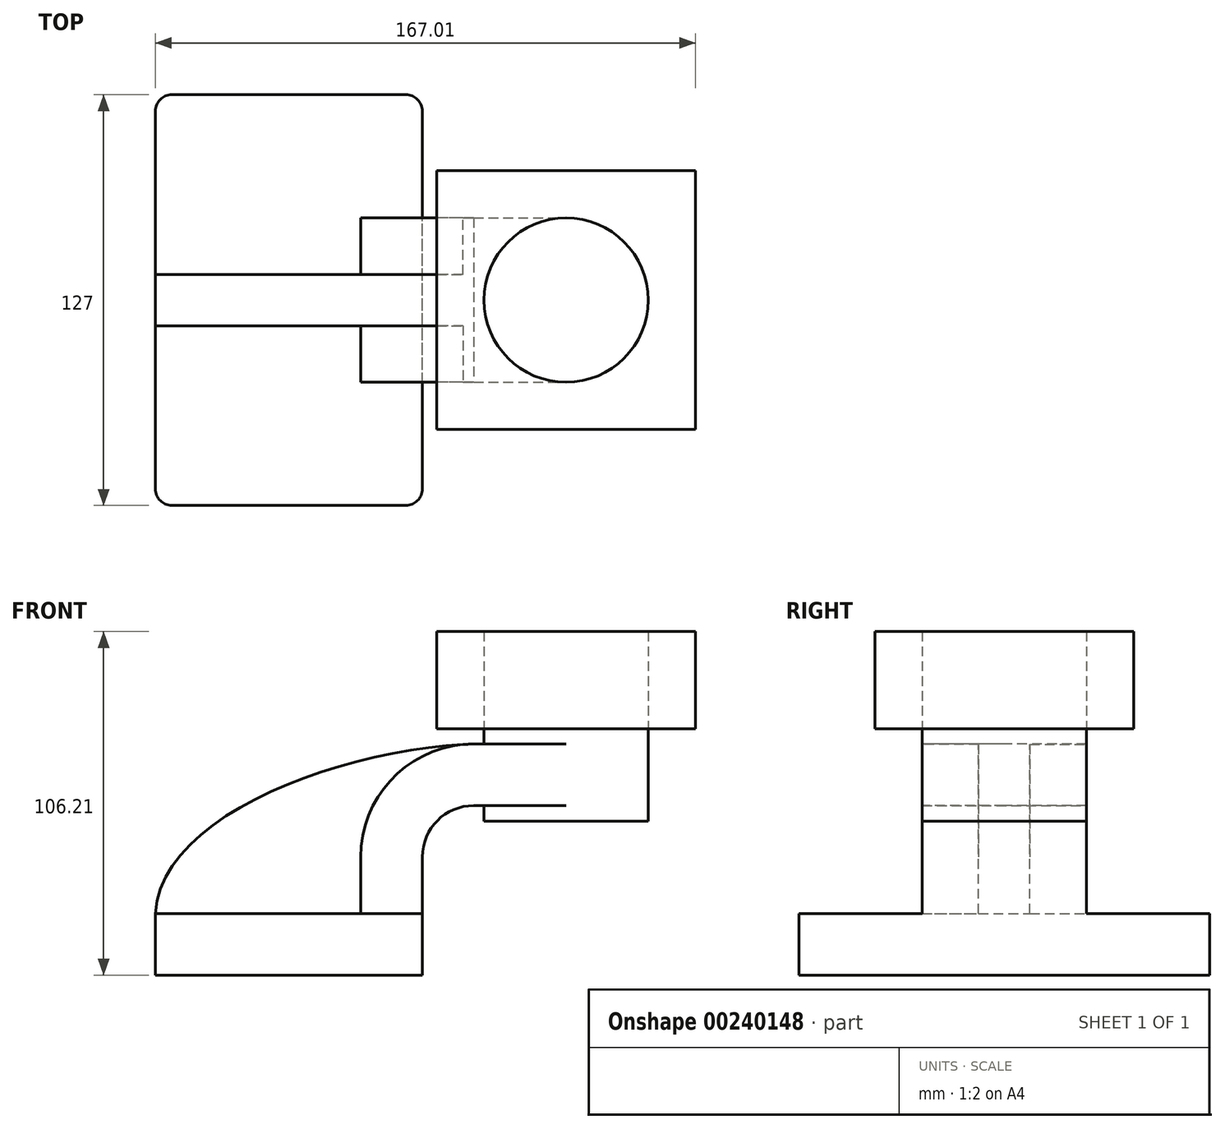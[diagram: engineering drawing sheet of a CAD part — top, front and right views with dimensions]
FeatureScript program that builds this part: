
annotation { "Feature Type Name" : "Feature", "Feature Type Description" : "" }
export const myFeature = defineFeature(function(context is Context, id is Id, definition is map)
    precondition{}
    {
        {
            var Q0;
            Q0=qCreatedBy(makeId("Front.planeOp"),FACE);
            var sketch = newSketch(context, id + "F0", { "sketchPlane" : qUnion([Q0])});
            skLineSegment(sketch, "E0.rect.bottom", {"start": v(-41.28, 9.52) * mm, "end": v(41.28, 9.52) * mm});
            skLineSegment(sketch, "E0.rect.top", {"start": v(-41.28, -9.52) * mm, "end": v(41.28, -9.52) * mm});
            skLineSegment(sketch, "E0.rect.left", {"start": v(-41.28, 9.52) * mm, "end": v(-41.28, -9.52) * mm});
            skLineSegment(sketch, "E0.rect.right", {"start": v(41.28, 9.52) * mm, "end": v(41.28, -9.52) * mm});
            skPoint(sketch, "E0.rect.middle", {"position": v(0, 0) * mm});
            skLineSegment(sketch, "E1", {"start": v(41.28, 9.52) * mm, "end": v(41.28, 27) * mm});
            skArc(sketch, "E2", {"start": v(41.28, 27) * mm, "mid": v(45.92, 38.23) * mm, "end": v(57.15, 42.88) * mm});
            skLineSegment(sketch, "E3", {"start": v(57.15, 42.88) * mm, "end": v(85.72, 42.88) * mm});
            skLineSegment(sketch, "E4.rect.bottom", {"start": v(60.32, 38.1) * mm, "end": v(111.12, 38.1) * mm});
            skLineSegment(sketch, "E4.rect.top", {"start": v(60.32, 66.68) * mm, "end": v(111.12, 66.68) * mm});
            skLineSegment(sketch, "E4.rect.left", {"start": v(60.32, 38.1) * mm, "end": v(60.32, 66.68) * mm});
            skLineSegment(sketch, "E4.rect.right", {"start": v(111.13, 38.1) * mm, "end": v(111.12, 66.68) * mm});
            skPoint(sketch, "E4.rect.middle", {"position": v(85.72, 52.39) * mm});
            skLineSegment(sketch, "E5.0", {"start": v(57.15, 61.93) * mm, "end": v(85.72, 61.93) * mm});
            skArc(sketch, "E5.1", {"start": v(22.23, 27) * mm, "mid": v(32.45, 51.7) * mm, "end": v(57.15, 61.93) * mm});
            skLineSegment(sketch, "E5.2", {"start": v(22.23, 9.52) * mm, "end": v(22.23, 27) * mm});
            skLineSegment(sketch, "E6", {"start": v(85.72, 38.1) * mm, "end": v(85.72, 66.68) * mm});
            skFitSpline(sketch, "E7", {"points": [v(-41.28, 9.53) * mm, v(57.15, 61.93) * mm], "startDerivative": vector(5.2, 92.34) * mm, "endDerivative": vector(120.92, 4.22) * mm});
            skSolve(sketch);
        }
        {
            var Q0;
            Q0=makeQuery(id+"F0.imprint","IMPRINT",FACE,{"disambiguationData":[TD([[makeQuery(id+"F0.imprint","IMPRINT",EDGE,{"derivedFrom":sQuery(id+"F0.wireOp",EDGE,"E0.rect.top")}),1.0]])]});
            extrude(context, id + "F1", {"entities" : qUnion([Q0]), "endBound" : BoundingType.SYMMETRIC, "depth" : 127 * mm});
        }
        {
            var Q0;
            {var subQ9=sQuery(id+"F0.wireOp",EDGE,"E1");Q0=makeQuery(id+"F0.imprint","IMPRINT",FACE,{"disambiguationData":[TD([[makeQuery(id+"F0.imprint","IMPRINT",EDGE,{"derivedFrom":subQ9}),1.0]])]});}
            var Q1;
            {var subQ0=sQuery(id+"F0.wireOp",EDGE,"E6");var subQ1=sQuery(id+"F0.wireOp",EDGE,"E3");var subQ2=makeQuery(id+"F0.imprint","INTERSECT",VERTEX,{"derivedFrom":[subQ1,subQ0]});Q1=makeQuery(id+"F0.imprint","IMPRINT",FACE,{"disambiguationData":[TD([[makeQuery(id+"F0.imprint","IMPRINT",EDGE,{"disambiguationData":[TD([[subQ2,1.0]])],"derivedFrom":subQ1}),1.0]])]});}
            extrude(context, id + "F2", {"entities" : qUnion([Q0, Q1]), "operationType" : NewBodyOperationType.ADD, "endBound" : BoundingType.SYMMETRIC, "depth" : 50.8 * mm});
        }
        {
            var Q0;
            {var subQ3=sQuery(id+"F0.wireOp",EDGE,"E5.2");Q0=makeQuery(id+"F0.imprint","IMPRINT",FACE,{"disambiguationData":[TD([[makeQuery(id+"F0.imprint","IMPRINT",EDGE,{"derivedFrom":subQ3}),1.0]])]});}
            extrude(context, id + "F3", {"entities" : qUnion([Q0]), "operationType" : NewBodyOperationType.ADD, "endBound" : BoundingType.SYMMETRIC, "depth" : 15.88 * mm});
        }
        {
            var Q0;
            {var subQ5=sQuery(id+"F0.wireOp",EDGE,"E4.rect.right");Q0=makeQuery(id+"F0.imprint","IMPRINT",FACE,{"disambiguationData":[TD([[makeQuery(id+"F0.imprint","IMPRINT",EDGE,{"derivedFrom":subQ5}),1.0]])]});}
            var Q1;
            Q1=sQuery(id+"F0.wireOp",EDGE,"E6");
            revolve(context, id + "F4", {"operationType" : NewBodyOperationType.ADD, "entities" : qUnion([Q0]), "axis" : qUnion([Q1]), "revolveType" : RevolveType.FULL});
        }
        {
            var Q0;
            Q0=makeQuery(id+"F1.opExtrude","CAP_EDGE",EDGE,{"disambiguationData":[OSD([sQuery(id+"F0.wireOp",EDGE,"E0.rect.right")])],"isStart":false});
            var Q1;
            Q1=makeQuery(id+"F1.opExtrude","CAP_EDGE",EDGE,{"disambiguationData":[OSD([sQuery(id+"F0.wireOp",EDGE,"E0.rect.left")])],"isStart":false});
            var Q2;
            Q2=makeQuery(id+"F1.opExtrude","CAP_EDGE",EDGE,{"disambiguationData":[OSD([sQuery(id+"F0.wireOp",EDGE,"E0.rect.right")])],"isStart":true});
            var Q3;
            Q3=makeQuery(id+"F1.opExtrude","CAP_EDGE",EDGE,{"disambiguationData":[OSD([sQuery(id+"F0.wireOp",EDGE,"E0.rect.left")])],"isStart":true});
            fillet(context, id + "F5", {"entities" : qUnion([Q0, Q1, Q2, Q3]), "radius" : 5.08 * mm, "tangentPropagation" : true, "allowEdgeOverflow" : false});
        }
        {
            var Q0;
            Q0=makeQuery(id+"F4.opRevolve","SWEPT_FACE",FACE,{"disambiguationData":[OSD([sQuery(id+"F0.wireOp",EDGE,"E4.rect.top")])]});
            var sketch = newSketch(context, id + "F6", { "sketchPlane" : qUnion([Q0])});
            skLineSegment(sketch, "E8.bottom", {"start": v(125.73, 40) * mm, "end": v(45.73, 40) * mm});
            skLineSegment(sketch, "E8.top", {"start": v(125.73, -40) * mm, "end": v(45.73, -40) * mm});
            skLineSegment(sketch, "E8.left", {"start": v(125.73, 40) * mm, "end": v(125.73, -40) * mm});
            skLineSegment(sketch, "E8.right", {"start": v(45.73, 40) * mm, "end": v(45.73, -40) * mm});
            skPoint(sketch, "E8.middle", {"position": v(85.72, 0) * mm});
            skPoint(sketch, "E9", {"position": v(125.73, 0) * mm});
            skPoint(sketch, "E10", {"position": v(45.73, 0) * mm});
            skCircle(sketch, "E11", {"center": v(85.72, 0) * mm, "radius": 25.4 * mm});
            skPoint(sketch, "E11.first.point", {"position": v(86.43, 25.4) * mm});
            skPoint(sketch, "E11.second.point", {"position": v(110.21, -6.76) * mm});
            skPoint(sketch, "E11.third.point", {"position": v(67.56, -17.76) * mm});
            skSolve(sketch);
        }
        {
            var Q0;
            Q0 = qSketchRegion(id + "F6", true);
            extrude(context, id + "F7", {"entities" : qUnion([Q0]), "depth" : 30 * mm});
        }
    });
